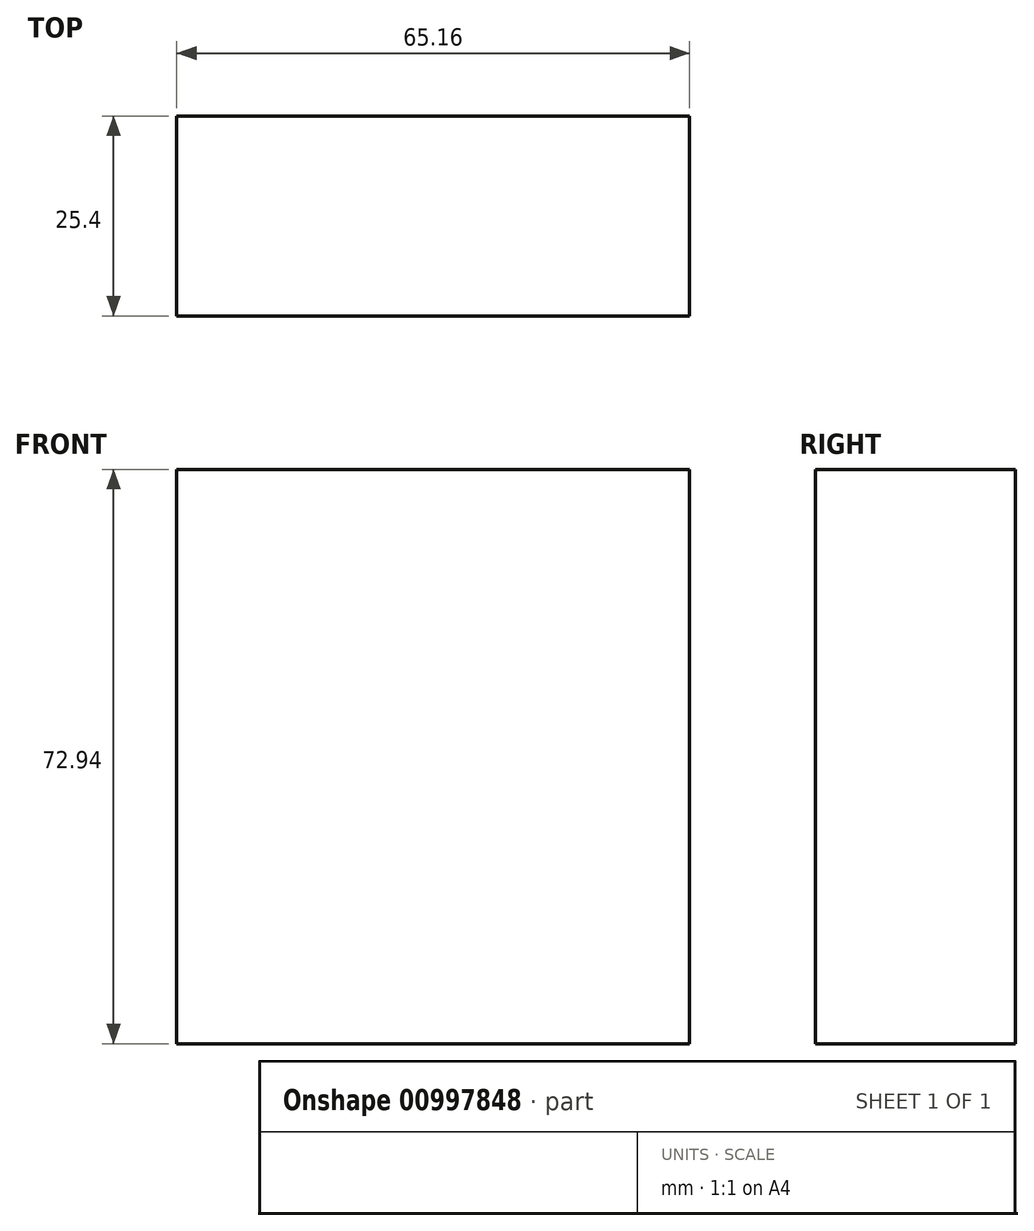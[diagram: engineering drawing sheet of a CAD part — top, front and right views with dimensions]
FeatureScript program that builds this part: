
annotation { "Feature Type Name" : "Feature", "Feature Type Description" : "" }
export const myFeature = defineFeature(function(context is Context, id is Id, definition is map)
    precondition{}
    {
        {
            var Q0;
            Q0=qCreatedBy(makeId("Front.planeOp"),FACE);
            var sketch = newSketch(context, id + "F0", { "sketchPlane" : qUnion([Q0])});
            skLineSegment(sketch, "E0.bottom", {"start": v(38.57, 24.55) * mm, "end": v(103.73, 24.55) * mm});
            skLineSegment(sketch, "E0.top", {"start": v(38.57, -48.4) * mm, "end": v(103.73, -48.4) * mm});
            skLineSegment(sketch, "E0.left", {"start": v(38.57, 24.55) * mm, "end": v(38.57, -48.4) * mm});
            skLineSegment(sketch, "E0.right", {"start": v(103.73, 24.55) * mm, "end": v(103.73, -48.4) * mm});
            skSolve(sketch);
        }
        {
            var Q0;
            Q0 = qSketchRegion(id + "F0", true);
            extrude(context, id + "F1", {"entities" : qUnion([Q0]), "depth" : 25.4 * mm, "offsetDistance" : 25.4 * mm});
        }
    });
